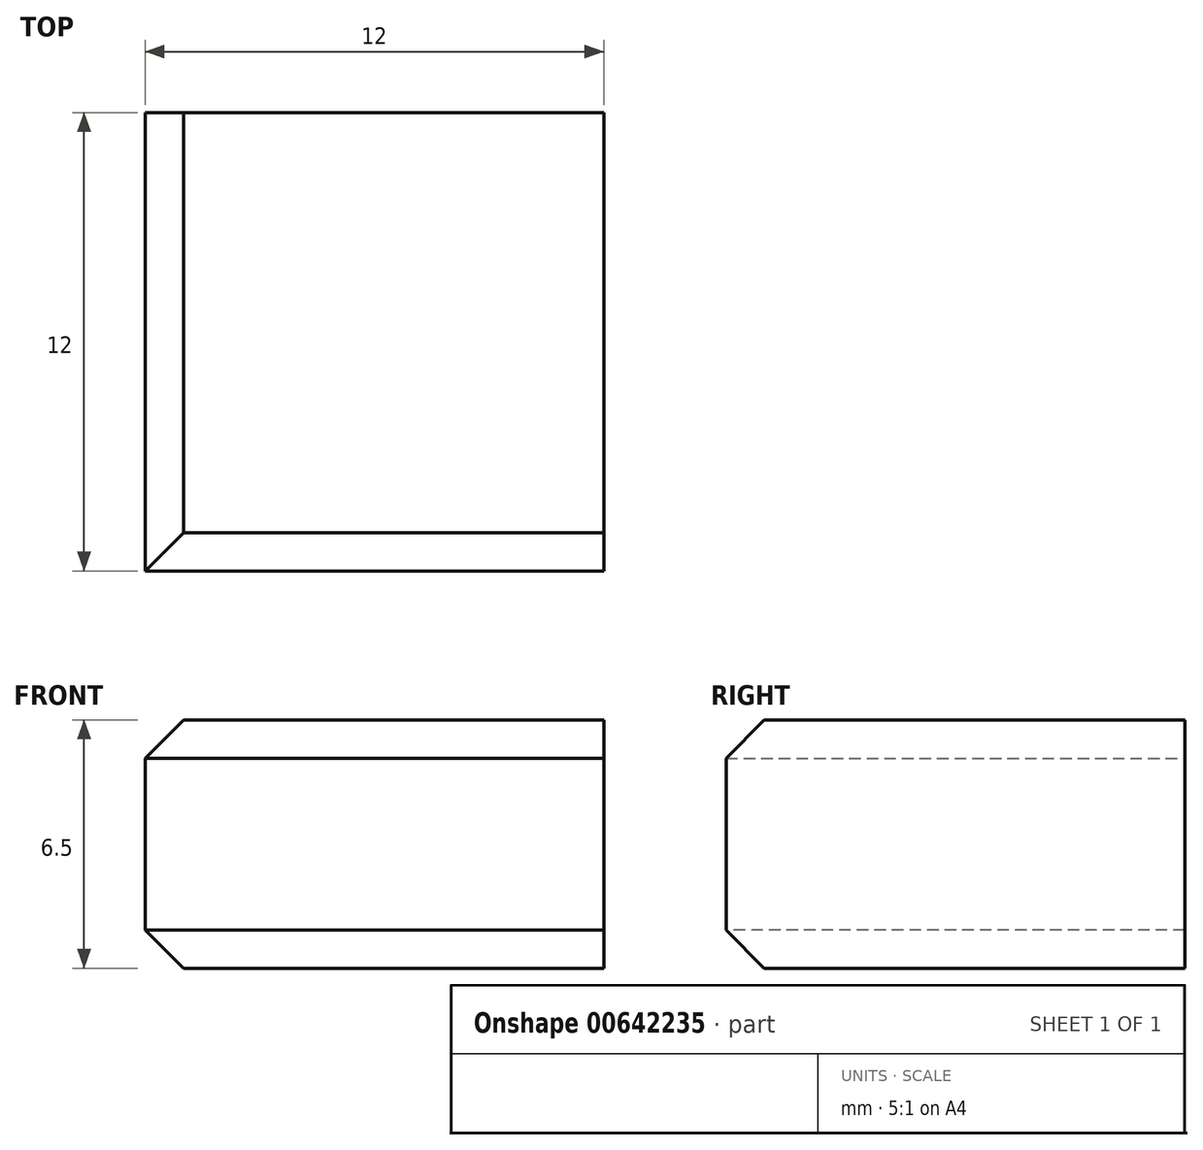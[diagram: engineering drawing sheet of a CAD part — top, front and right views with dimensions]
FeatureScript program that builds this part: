
annotation { "Feature Type Name" : "Feature", "Feature Type Description" : "" }
export const myFeature = defineFeature(function(context is Context, id is Id, definition is map)
    precondition{}
    {
        {
            var Q0;
            Q0=qCreatedBy(makeId("Top.planeOp"),FACE);
            var sketch = newSketch(context, id + "F0", { "sketchPlane" : qUnion([Q0])});
            skLineSegment(sketch, "E0.bottom", {"start": v(0, 0) * mm, "end": v(30, 0) * mm});
            skLineSegment(sketch, "E0.top", {"start": v(0, 60) * mm, "end": v(30, 60) * mm});
            skLineSegment(sketch, "E0.left", {"start": v(0, 0) * mm, "end": v(0, 60) * mm});
            skLineSegment(sketch, "E0.right", {"start": v(30, 0) * mm, "end": v(30, 60) * mm});
            skLineSegment(sketch, "E1.bottom", {"start": v(0, 0) * mm, "end": v(12, 0) * mm});
            skLineSegment(sketch, "E1.top", {"start": v(0, 12) * mm, "end": v(12, 12) * mm});
            skLineSegment(sketch, "E1.left", {"start": v(0, 0) * mm, "end": v(0, 12) * mm});
            skLineSegment(sketch, "E1.right", {"start": v(12, 0) * mm, "end": v(12, 12) * mm});
            skCircle(sketch, "E2", {"center": v(25, 55) * mm, "radius": 2 * mm});
            skCircle(sketch, "E3.0.1.0", {"center": v(25, 9) * mm, "radius": 2 * mm});
            skLineSegment(sketch, "E3.direction1", {"start": v(25, 55) * mm, "end": v(50, 55) * mm, "construction": true});
            skLineSegment(sketch, "E3.direction2", {"start": v(25, 55) * mm, "end": v(25, 9) * mm, "construction": true});
            skSolve(sketch);
        }
        {
            var Q0;
            Q0=makeQuery(id+"F0.imprint","IMPRINT",FACE,{"disambiguationData":[TD([[makeQuery(id+"F0.imprint","IMPRINT",EDGE,{"derivedFrom":sQuery(id+"F0.wireOp",EDGE,"E0.bottom")}),1.0]])]});
            var Q1;
            Q1=makeQuery(id+"F0.imprint","IMPRINT",FACE,{"disambiguationData":[TD([[makeQuery(id+"F0.imprint","IMPRINT",EDGE,{"derivedFrom":sQuery(id+"F0.wireOp",EDGE,"EaJcMfvd-O72H-BCZg-WxpM-z2a6Eh5W0zUc.bottom")}),1.0]])]});
            var Q2;
            Q2=makeQuery(id+"F0.imprint","IMPRINT",FACE,{"disambiguationData":[TD([[makeQuery(id+"F0.imprint","IMPRINT",EDGE,{"derivedFrom":sQuery(id+"F0.wireOp",EDGE,"iRwnBI1Y-z3Nr-Pozh-xLRk-Ro8O9V2kgngy.bottom")}),1.0]])]});
            extrude(context, id + "F1", {"entities" : qUnion([Q0, Q1, Q2]), "depth" : 6.5 * mm, "offsetDistance" : 25 * mm});
        }
        {
            var Q0;
            Q0=makeQuery(id+"F1.opExtrude","CAP_EDGE",EDGE,{"disambiguationData":[OSD([sQuery(id+"F0.wireOp",EDGE,"E0.bottom")])],"isStart":true});
            var Q1;
            Q1=makeQuery(id+"F1.opExtrude","CAP_EDGE",EDGE,{"disambiguationData":[OSD([sQuery(id+"F0.wireOp",EDGE,"E0.bottom")])],"isStart":false});
            var Q2;
            Q2=makeQuery(id+"F1.opExtrude","CAP_EDGE",EDGE,{"disambiguationData":[OSD([sQuery(id+"F0.wireOp",EDGE,"E0.left")])],"isStart":true});
            var Q3;
            Q3=makeQuery(id+"F1.opExtrude","CAP_EDGE",EDGE,{"disambiguationData":[OSD([sQuery(id+"F0.wireOp",EDGE,"E0.left")])],"isStart":false});
            chamfer(context, id + "F2", {"entities" : qUnion([Q0, Q1, Q2, Q3]), "width" : 1 * mm, "tangentPropagation" : true});
        }
    });
